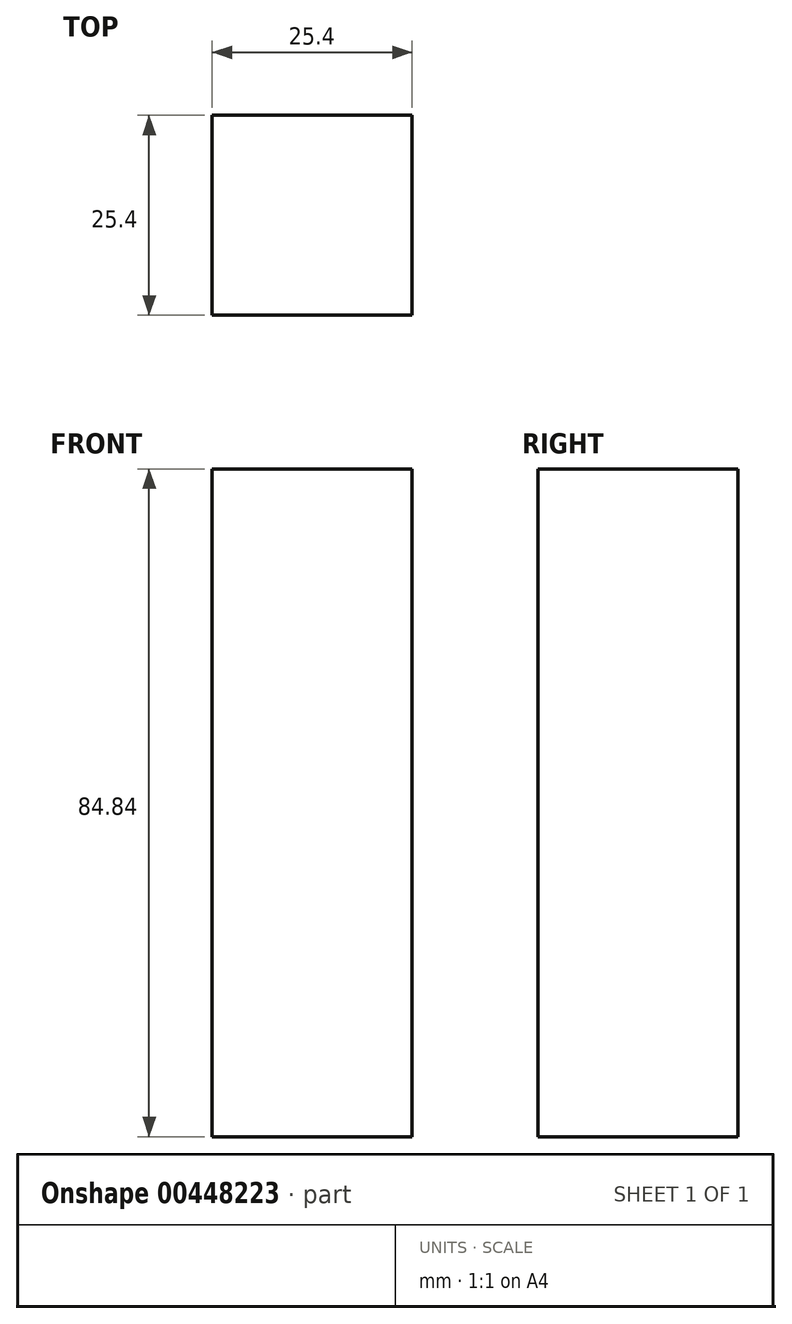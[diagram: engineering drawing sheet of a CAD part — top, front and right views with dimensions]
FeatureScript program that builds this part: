
annotation { "Feature Type Name" : "Feature", "Feature Type Description" : "" }
export const myFeature = defineFeature(function(context is Context, id is Id, definition is map)
    precondition{}
    {
        {
            var Q0;
            Q0=qCreatedBy(makeId("Top.planeOp"),FACE);
            var sketch = newSketch(context, id + "F0", { "sketchPlane" : qUnion([Q0])});
            skLineSegment(sketch, "E0.bottom", {"start": v(0, 0) * mm, "end": v(25.4, 0) * mm});
            skLineSegment(sketch, "E0.top", {"start": v(0, 25.4) * mm, "end": v(25.4, 25.4) * mm});
            skLineSegment(sketch, "E0.left", {"start": v(0, 0) * mm, "end": v(0, 25.4) * mm});
            skLineSegment(sketch, "E0.right", {"start": v(25.4, 0) * mm, "end": v(25.4, 25.4) * mm});
            skSolve(sketch);
        }
        {
            var Q0;
            Q0=makeQuery(id+"F0.imprint","IMPRINT",FACE,{"disambiguationData":[TD([[makeQuery(id+"F0.imprint","IMPRINT",EDGE,{"derivedFrom":sQuery(id+"F0.wireOp",EDGE,"E0.bottom")}),1.0]])]});
            extrude(context, id + "F1", {"entities" : qUnion([Q0]), "depth" : 84.84 * mm});
        }
    });
